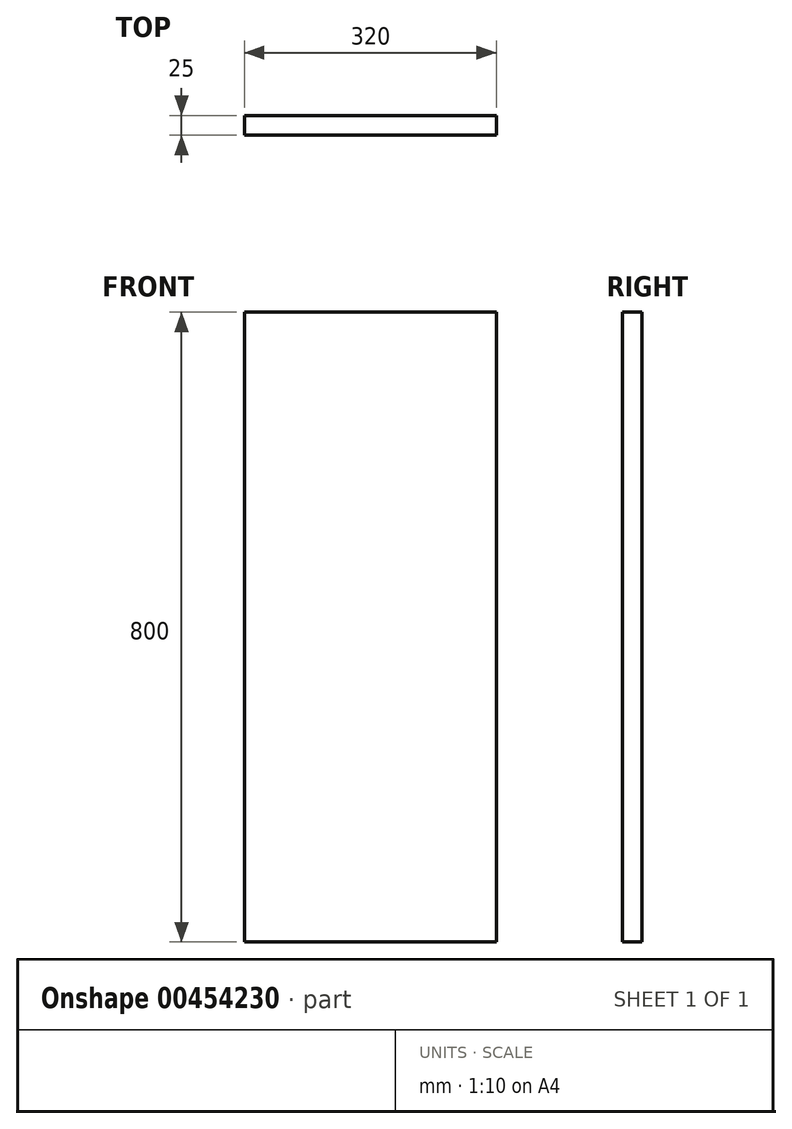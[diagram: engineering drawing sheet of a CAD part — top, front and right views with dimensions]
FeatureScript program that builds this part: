
annotation { "Feature Type Name" : "Feature", "Feature Type Description" : "" }
export const myFeature = defineFeature(function(context is Context, id is Id, definition is map)
    precondition{}
    {
        {
            var Q0;
            Q0=qCreatedBy(makeId("Front.planeOp"),FACE);
            var sketch = newSketch(context, id + "F0", { "sketchPlane" : qUnion([Q0])});
            skLineSegment(sketch, "E0.bottom", {"start": v(-160, -400) * mm, "end": v(160, -400) * mm});
            skLineSegment(sketch, "E0.top", {"start": v(-160, 400) * mm, "end": v(160, 400) * mm});
            skLineSegment(sketch, "E0.left", {"start": v(-160, -400) * mm, "end": v(-160, 400) * mm});
            skLineSegment(sketch, "E0.right", {"start": v(160, -400) * mm, "end": v(160, 400) * mm});
            skPoint(sketch, "E0.middle", {"position": v(0, 0) * mm});
            skSolve(sketch);
        }
        {
            var Q0;
            Q0 = qSketchRegion(id + "F0", true);
            extrude(context, id + "F1", {"entities" : qUnion([Q0]), "depth" : 25 * mm});
        }
    });
